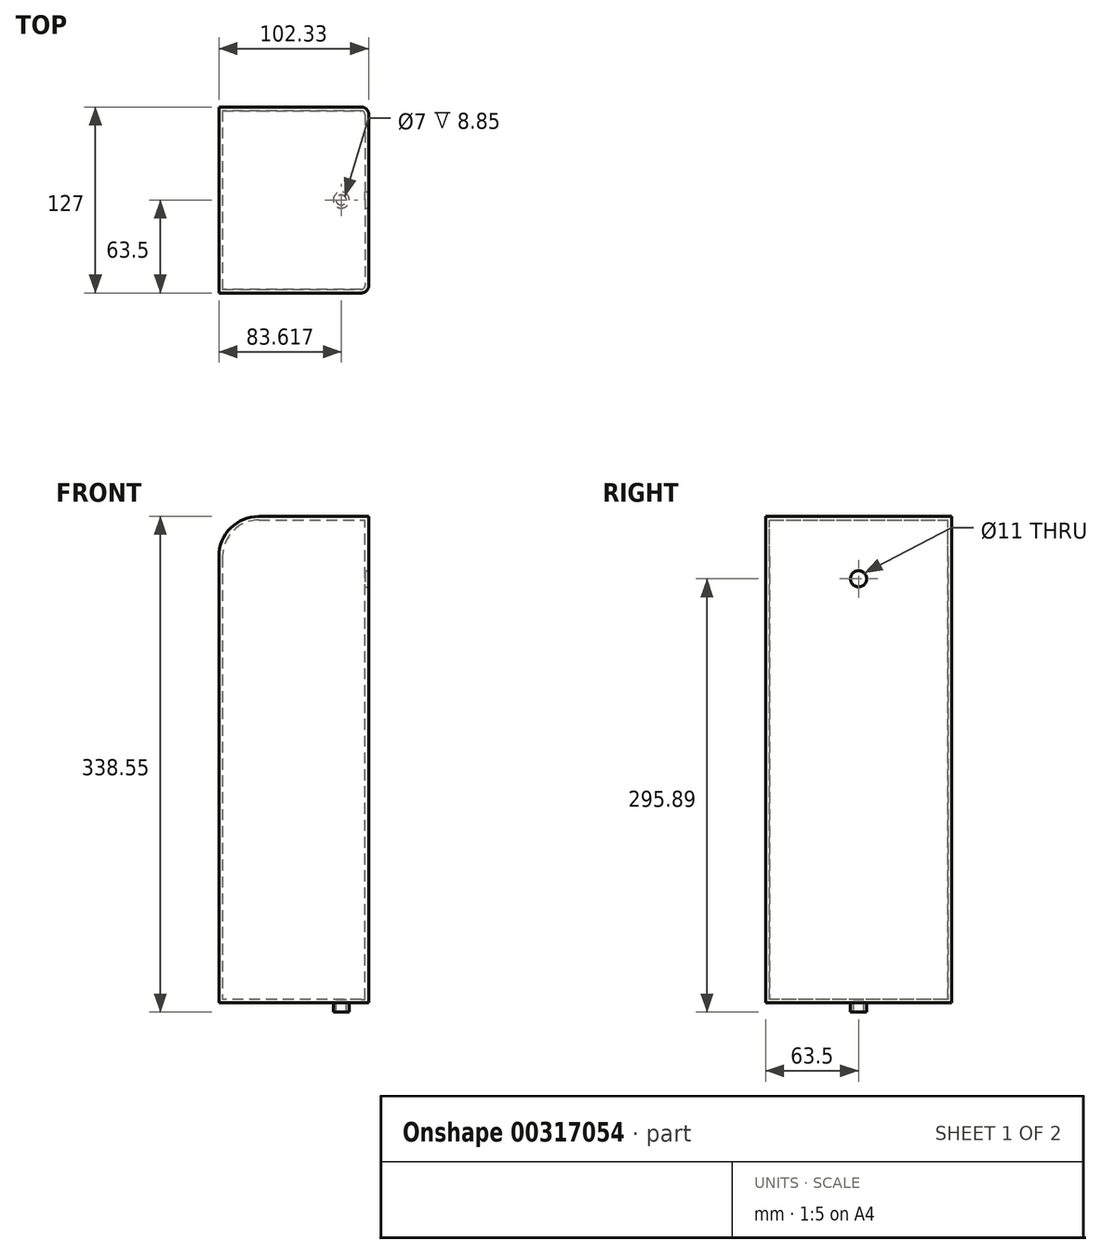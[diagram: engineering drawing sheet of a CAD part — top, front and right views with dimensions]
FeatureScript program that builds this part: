
annotation { "Feature Type Name" : "Feature", "Feature Type Description" : "" }
export const myFeature = defineFeature(function(context is Context, id is Id, definition is map)
    precondition{}
    {
        {
            var Q0;
            Q0=qCreatedBy(makeId("Top.planeOp"),FACE);
            var sketch = newSketch(context, id + "F0", { "sketchPlane" : qUnion([Q0])});
            skLineSegment(sketch, "E0.bottom", {"start": v(0, 0) * mm, "end": v(102.33, 0) * mm});
            skLineSegment(sketch, "E0.top", {"start": v(0, 127) * mm, "end": v(102.33, 127) * mm});
            skLineSegment(sketch, "E0.left", {"start": v(0, 0) * mm, "end": v(0, 127) * mm});
            skLineSegment(sketch, "E0.right", {"start": v(102.33, 0) * mm, "end": v(102.33, 127) * mm});
            skSolve(sketch);
        }
        {
            var Q0;
            Q0 = qSketchRegion(id + "F0", true);
            extrude(context, id + "F1", {"entities" : qUnion([Q0]), "depth" : 330.2 * mm + 2 * mm});
        }
        {
            var Q0;
            Q0=makeQuery(id+"F1.opExtrude","CAP_EDGE",EDGE,{"disambiguationData":[OSD([sQuery(id+"F0.wireOp",EDGE,"E0.left")])],"isStart":false});
            fillet(context, id + "F2", {"entities" : qUnion([Q0]), "radius" : 27.4 * mm, "tangentPropagation" : true, "allowEdgeOverflow" : false});
        }
        {
            var Q0;
            Q0=makeQuery(id+"F1.opExtrude","SWEPT_EDGE",EDGE,{"disambiguationData":[OSD([sQuery(id+"F0.wireOp",EDGE,"E0.bottom"),sQuery(id+"F0.wireOp",EDGE,"E0.right")])]});
            var Q1;
            Q1=makeQuery(id+"F1.opExtrude","SWEPT_EDGE",EDGE,{"disambiguationData":[OSD([sQuery(id+"F0.wireOp",EDGE,"E0.top"),sQuery(id+"F0.wireOp",EDGE,"E0.right")])]});
            fillet(context, id + "F3", {"entities" : qUnion([Q0, Q1]), "radius" : 5.08 * mm, "tangentPropagation" : true, "allowEdgeOverflow" : false});
        }
        {
            var Q0;
            Q0=makeQuery(id+"F1.opExtrude","SWEPT_FACE",FACE,{"disambiguationData":[OSD([sQuery(id+"F0.wireOp",EDGE,"E0.right")])]});
            var sketch = newSketch(context, id + "F4", { "sketchPlane" : qUnion([Q0])});
            skCircle(sketch, "E1", {"center": v(63.5, 289.54) * mm, "radius": 5.5 * mm});
            skPoint(sketch, "E1.centerSnap0", {"position": v(63.5, 332.2) * mm});
            skSolve(sketch);
        }
        {
            var Q0;
            Q0=makeQuery(id+"F1.opExtrude","CAP_FACE",FACE,{"disambiguationData":[OSD([sQuery(id+"F0.wireOp",EDGE,"E0.bottom"),sQuery(id+"F0.wireOp",EDGE,"E0.top"),sQuery(id+"F0.wireOp",EDGE,"E0.left"),sQuery(id+"F0.wireOp",EDGE,"E0.right")])],"isStart":true});
            shell(context, id + "F5", {"entities" : qUnion([Q0]), "thickness" : 2.5 * mm});
        }
        {
            var Q0;
            Q0=makeQuery(id+"F1.opExtrude","CAP_FACE",FACE,{"disambiguationData":[OSD([sQuery(id+"F0.wireOp",EDGE,"E0.bottom"),sQuery(id+"F0.wireOp",EDGE,"E0.top"),sQuery(id+"F0.wireOp",EDGE,"E0.left"),sQuery(id+"F0.wireOp",EDGE,"E0.right")])],"isStart":true});
            var sketch = newSketch(context, id + "F6", { "sketchPlane" : qUnion([Q0])});
            skLineSegment(sketch, "E2.0", {"start": v(102.33, -5.08) * mm, "end": v(102.33, -121.92) * mm});
            skLineSegment(sketch, "E3.0", {"start": v(0, -127) * mm, "end": v(97.25, -127) * mm});
            skLineSegment(sketch, "E4.0", {"start": v(0, 0) * mm, "end": v(0, -127) * mm});
            skLineSegment(sketch, "E5.0", {"start": v(0, 0) * mm, "end": v(97.25, 0) * mm});
            skArc(sketch, "E6.0", {"start": v(102.33, -5.08) * mm, "mid": v(100.84, -1.49) * mm, "end": v(97.25, 0) * mm});
            skArc(sketch, "E7.0", {"start": v(97.25, -127) * mm, "mid": v(100.84, -125.51) * mm, "end": v(102.33, -121.92) * mm});
            skSolve(sketch);
        }
        {
            var Q0;
            Q0 = qSketchRegion(id + "F6", true);
            extrude(context, id + "F7", {"entities" : qUnion([Q0]), "operationType" : NewBodyOperationType.ADD, "oppositeDirection" : true, "depth" : 2.5 * mm});
        }
        {
            var Q0;
            Q0 = qSketchRegion(id + "F4", true);
            extrude(context, id + "F8", {"entities" : qUnion([Q0]), "operationType" : NewBodyOperationType.REMOVE, "endBound" : BoundingType.UP_TO_NEXT, "oppositeDirection" : true, "depth" : 25.4 * mm});
        }
        {
            var Q0;
            Q0=makeQuery(id+"F7.boolean.opBoolean","MERGE",FACE,{"derivedFrom":[makeQuery(id+"F1.opExtrude","CAP_FACE",FACE,{"disambiguationData":[OSD([sQuery(id+"F0.wireOp",EDGE,"E0.bottom"),sQuery(id+"F0.wireOp",EDGE,"E0.top"),sQuery(id+"F0.wireOp",EDGE,"E0.left"),sQuery(id+"F0.wireOp",EDGE,"E0.right")])],"isStart":true}),makeQuery(id+"F7.opExtrude","CAP_FACE",FACE,{"disambiguationData":[OSD([sQuery(id+"F6.wireOp",EDGE,"E2.0"),sQuery(id+"F6.wireOp",EDGE,"E3.0"),sQuery(id+"F6.wireOp",EDGE,"E4.0"),sQuery(id+"F6.wireOp",EDGE,"E5.0"),sQuery(id+"F6.wireOp",EDGE,"E6.0"),sQuery(id+"F6.wireOp",EDGE,"E7.0")])],"isStart":true})]});
            var sketch = newSketch(context, id + "F9", { "sketchPlane" : qUnion([Q0])});
            skCircle(sketch, "E8", {"center": v(83.62, -63.5) * mm, "radius": 5.5 * mm});
            skPoint(sketch, "E8.centerSnap0", {"position": v(102.33, -63.5) * mm});
            skCircle(sketch, "E9", {"center": v(83.62, -63.5) * mm, "radius": 3.5 * mm});
            skSolve(sketch);
        }
        {
            var Q0;
            Q0 = qSketchRegion(id + "F9", true);
            extrude(context, id + "F10", {"entities" : qUnion([Q0]), "operationType" : NewBodyOperationType.ADD, "depth" : 6.35 * mm});
        }
        {
            var Q0;
            Q0=makeQuery(id+"F10.boolean.opBoolean","SPLIT",FACE,{"disambiguationData":[TD([makeQuery(id+"F10.opExtrude","SWEPT_FACE",FACE,{"disambiguationData":[OSD([sQuery(id+"F9.wireOp",EDGE,"E9")])]})])],"derivedFrom":makeQuery(id+"F7.boolean.opBoolean","MERGE",FACE,{"derivedFrom":[makeQuery(id+"F1.opExtrude","CAP_FACE",FACE,{"disambiguationData":[OSD([sQuery(id+"F0.wireOp",EDGE,"E0.bottom"),sQuery(id+"F0.wireOp",EDGE,"E0.top"),sQuery(id+"F0.wireOp",EDGE,"E0.left"),sQuery(id+"F0.wireOp",EDGE,"E0.right")])],"isStart":true}),makeQuery(id+"F7.opExtrude","CAP_FACE",FACE,{"disambiguationData":[OSD([sQuery(id+"F6.wireOp",EDGE,"E2.0"),sQuery(id+"F6.wireOp",EDGE,"E3.0"),sQuery(id+"F6.wireOp",EDGE,"E4.0"),sQuery(id+"F6.wireOp",EDGE,"E5.0"),sQuery(id+"F6.wireOp",EDGE,"E6.0"),sQuery(id+"F6.wireOp",EDGE,"E7.0")])],"isStart":true})]})});
            extrude(context, id + "F11", {"entities" : qUnion([Q0]), "operationType" : NewBodyOperationType.REMOVE, "endBound" : BoundingType.UP_TO_NEXT, "oppositeDirection" : true, "depth" : 25.4 * mm});
        }
    });
